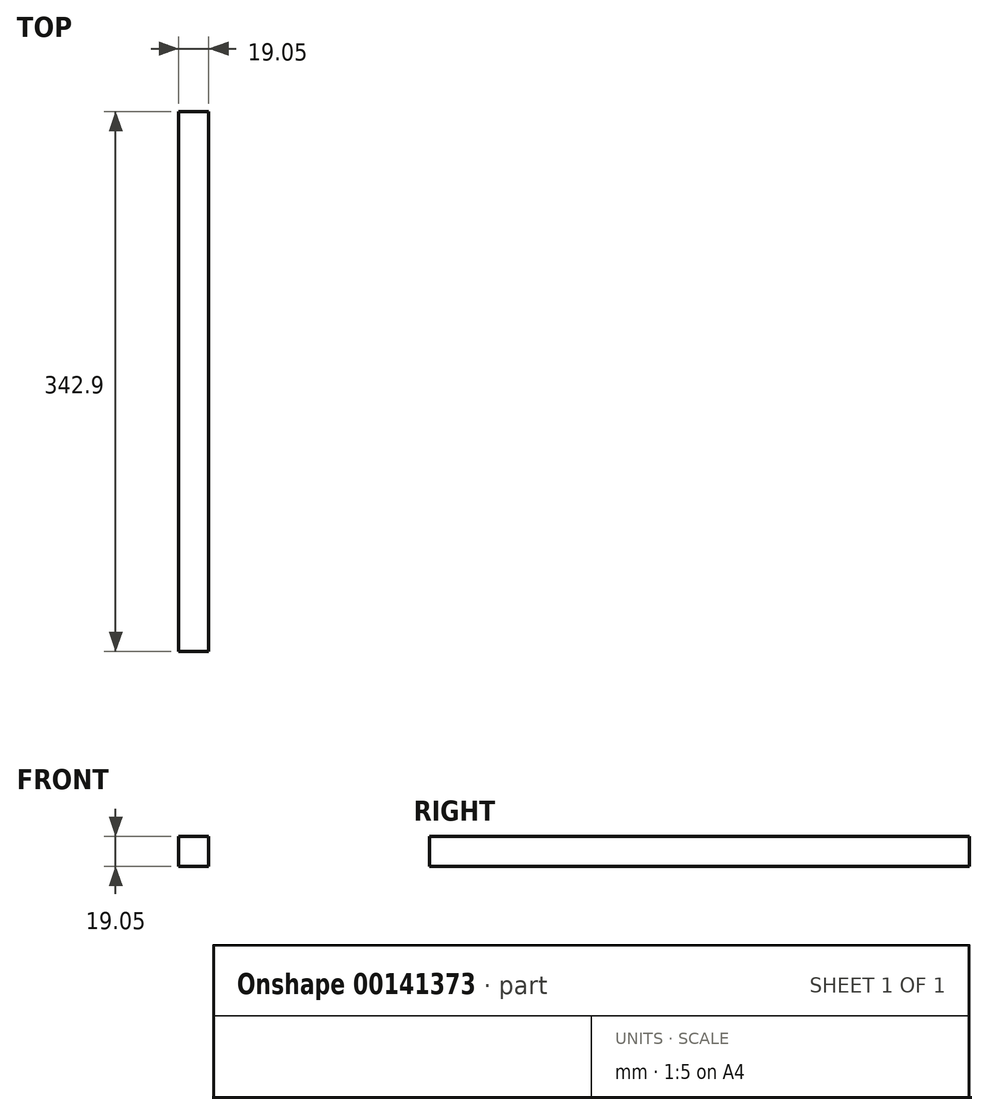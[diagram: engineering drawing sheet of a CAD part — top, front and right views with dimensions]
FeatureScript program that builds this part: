
annotation { "Feature Type Name" : "Feature", "Feature Type Description" : "" }
export const myFeature = defineFeature(function(context is Context, id is Id, definition is map)
    precondition{}
    {
        {
            var Q0;
            Q0=qCreatedBy(makeId("Top.planeOp"),FACE);
            var sketch = newSketch(context, id + "F0", { "sketchPlane" : qUnion([Q0])});
            skLineSegment(sketch, "E0.bottom", {"start": v(-83.4, -230.27) * mm, "end": v(-64.36, -230.27) * mm});
            skLineSegment(sketch, "E0.top", {"start": v(-83.4, 112.63) * mm, "end": v(-64.36, 112.63) * mm});
            skLineSegment(sketch, "E0.left", {"start": v(-83.4, -230.27) * mm, "end": v(-83.4, 112.63) * mm});
            skLineSegment(sketch, "E0.right", {"start": v(-64.36, -230.27) * mm, "end": v(-64.36, 112.63) * mm});
            skSolve(sketch);
        }
        {
            var Q0;
            Q0=makeQuery(id+"F0.imprint","IMPRINT",FACE,{"disambiguationData":[TD([[makeQuery(id+"F0.imprint","IMPRINT",EDGE,{"derivedFrom":sQuery(id+"F0.wireOp",EDGE,"E0.bottom")}),1.0]])]});
            extrude(context, id + "F1", {"entities" : qUnion([Q0]), "depth" : 19.05 * mm});
        }
    });
